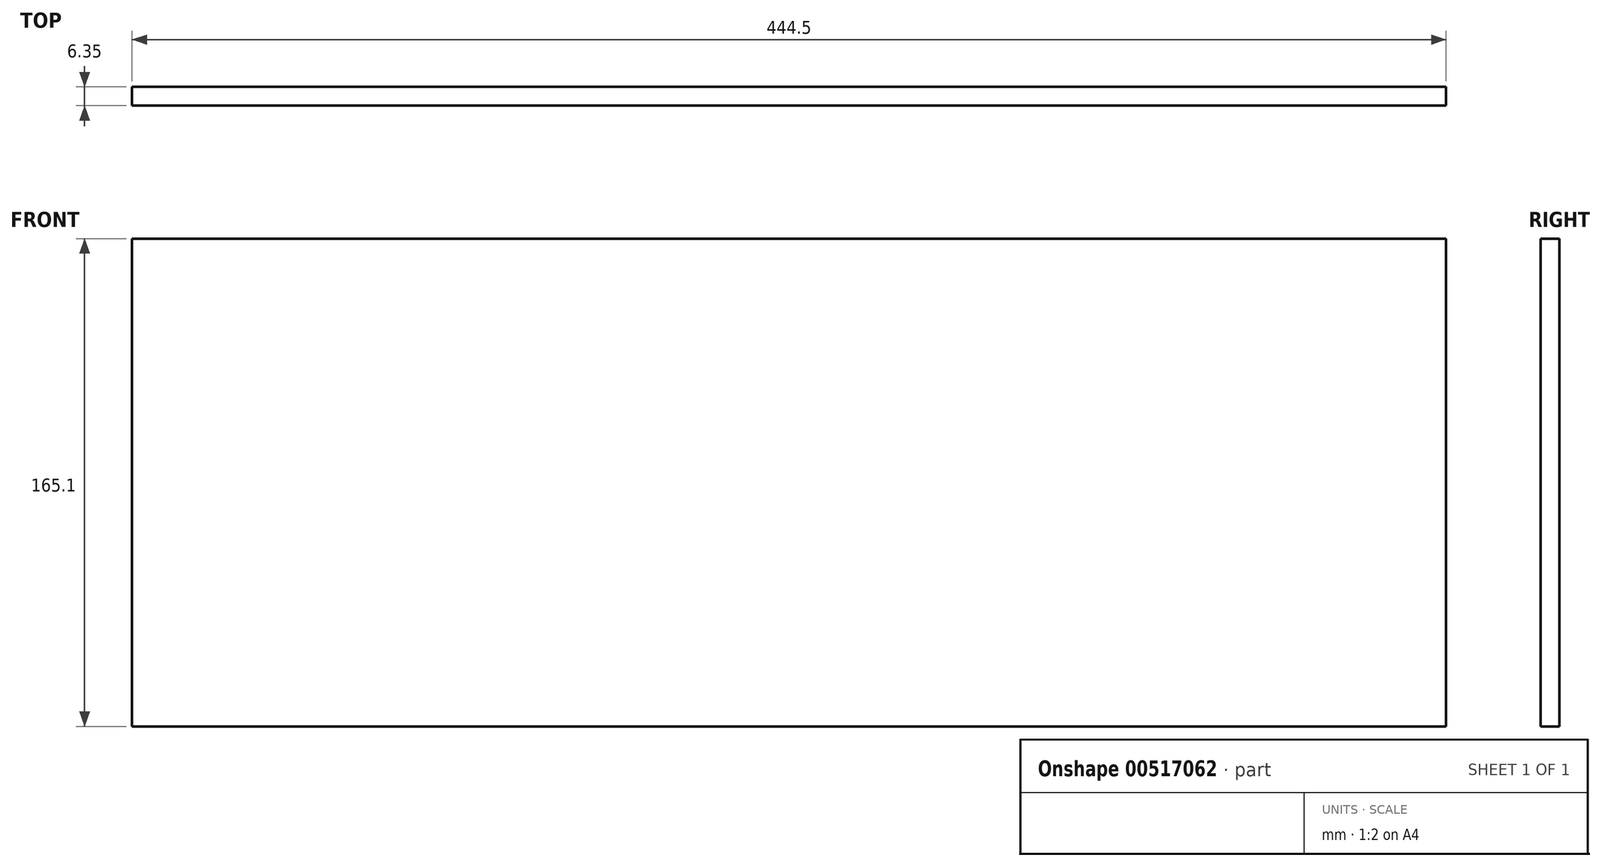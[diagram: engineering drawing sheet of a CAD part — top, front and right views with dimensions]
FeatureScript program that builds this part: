
annotation { "Feature Type Name" : "Feature", "Feature Type Description" : "" }
export const myFeature = defineFeature(function(context is Context, id is Id, definition is map)
    precondition{}
    {
        {
            var Q0;
            Q0=qCreatedBy(makeId("Front.planeOp"),FACE);
            var sketch = newSketch(context, id + "F0", { "sketchPlane" : qUnion([Q0])});
            skLineSegment(sketch, "E0.bottom", {"start": v(-240.9, 92.53) * mm, "end": v(203.6, 92.53) * mm});
            skLineSegment(sketch, "E0.top", {"start": v(-240.9, -72.57) * mm, "end": v(203.6, -72.57) * mm});
            skLineSegment(sketch, "E0.left", {"start": v(-240.9, 92.53) * mm, "end": v(-240.9, -72.57) * mm});
            skLineSegment(sketch, "E0.right", {"start": v(203.6, 92.53) * mm, "end": v(203.6, -72.57) * mm});
            skSolve(sketch);
        }
        {
            var Q0;
            Q0=makeQuery(id+"F0.imprint","IMPRINT",FACE,{"disambiguationData":[TD([[makeQuery(id+"F0.imprint","IMPRINT",EDGE,{"derivedFrom":sQuery(id+"F0.wireOp",EDGE,"E0.bottom")}),-1.0]])]});
            extrude(context, id + "F1", {"entities" : qUnion([Q0]), "depth" : 12.7 * mm, "offsetDistance" : 25.4 * mm});
        }
        {
            var Q0;
            Q0=makeQuery(id+"F1.opExtrude","CAP_FACE",FACE,{"disambiguationData":[OSD([sQuery(id+"F0.wireOp",EDGE,"E0.bottom"),sQuery(id+"F0.wireOp",EDGE,"E0.top"),sQuery(id+"F0.wireOp",EDGE,"E0.left"),sQuery(id+"F0.wireOp",EDGE,"E0.right")])],"isStart":false});
            extrude(context, id + "F2", {"entities" : qUnion([Q0]), "operationType" : NewBodyOperationType.REMOVE, "oppositeDirection" : true, "depth" : 6.35 * mm, "offsetDistance" : 25.4 * mm});
        }
    });
